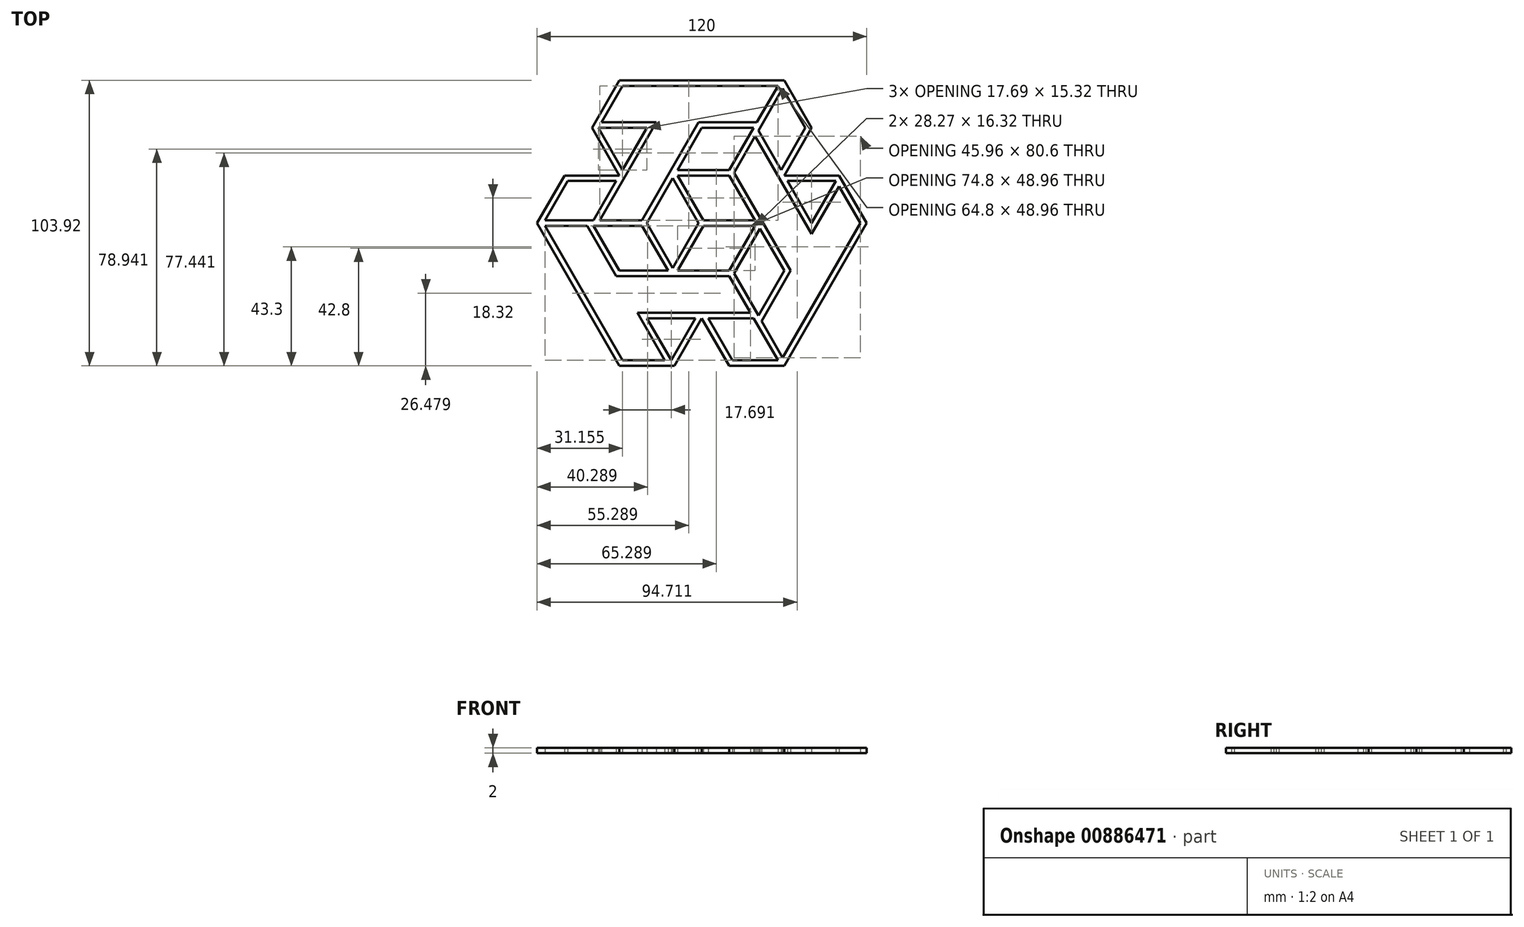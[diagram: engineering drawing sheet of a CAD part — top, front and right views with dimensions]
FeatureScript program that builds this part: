
annotation { "Feature Type Name" : "Feature", "Feature Type Description" : "" }
export const myFeature = defineFeature(function(context is Context, id is Id, definition is map)
    precondition{}
    {
        {
            var Q0;
            Q0=qCreatedBy(makeId("Top.planeOp"),FACE);
            var sketch = newSketch(context, id + "F0", { "sketchPlane" : qUnion([Q0])});
            skCircle(sketch, "E0.cCircle", {"center": v(0, 0) * mm, "radius": 60 * mm, "construction": true});
            skLineSegment(sketch, "E0.0", {"start": v(-60, 0) * mm, "end": v(-50, 17.32) * mm});
            skLineSegment(sketch, "E0.1", {"start": v(-30, 51.96) * mm, "end": v(30, 51.96) * mm});
            skLineSegment(sketch, "E0.2", {"start": v(30, 51.96) * mm, "end": v(60, 0) * mm});
            skLineSegment(sketch, "E0.3", {"start": v(60, 0) * mm, "end": v(30, -51.96) * mm});
            skLineSegment(sketch, "E0.4", {"start": v(30, -51.96) * mm, "end": v(-30, -51.96) * mm});
            skLineSegment(sketch, "E0.5", {"start": v(-30, -51.96) * mm, "end": v(-60, 0) * mm});
            skLineSegment(sketch, "E1", {"start": v(-20, 34.64) * mm, "end": v(-28.85, 19.32) * mm});
            skLineSegment(sketch, "E2", {"start": v(0, 34.64) * mm, "end": v(-8.85, 19.32) * mm});
            skLineSegment(sketch, "E3", {"start": v(-37.7, 34.64) * mm, "end": v(-20, 34.64) * mm});
            skLineSegment(sketch, "E4", {"start": v(-50, 17.32) * mm, "end": v(-30, 17.32) * mm});
            skPoint(sketch, "E5.orphan", {"position": v(-10, 51.96) * mm});
            skPoint(sketch, "E6.orphan", {"position": v(10, 51.96) * mm});
            skLineSegment(sketch, "E7.trimOffspring", {"start": v(0, 34.64) * mm, "end": v(18.85, 34.64) * mm});
            skLineSegment(sketch, "E8.trimOffspring", {"start": v(-8.85, 17.32) * mm, "end": v(10, 17.32) * mm});
            skLineSegment(sketch, "E9", {"start": v(-40, 34.64) * mm, "end": v(-30, 17.32) * mm});
            skLineSegment(sketch, "E10.trimOffspring", {"start": v(-40, 34.64) * mm, "end": v(-30, 51.96) * mm});
            skLineSegment(sketch, "E11.0", {"start": v(-16.54, 36.64) * mm, "end": v(-37.11, 1) * mm});
            skLineSegment(sketch, "E11.1", {"start": v(-36.54, 36.64) * mm, "end": v(-16.54, 36.64) * mm});
            skLineSegment(sketch, "E11.2", {"start": v(-36.54, 36.64) * mm, "end": v(-28.85, 49.96) * mm});
            skLineSegment(sketch, "E11.3", {"start": v(-28.85, 49.96) * mm, "end": v(27.7, 49.96) * mm});
            skLineSegment(sketch, "E12.0", {"start": v(-1.15, 36.64) * mm, "end": v(-21.73, 1) * mm});
            skLineSegment(sketch, "E12.1", {"start": v(-1.15, 36.64) * mm, "end": v(20, 36.64) * mm});
            skLineSegment(sketch, "E13.1", {"start": v(27.7, 49.96) * mm, "end": v(20, 36.64) * mm});
            skLineSegment(sketch, "E14.0", {"start": v(-37.7, 34.64) * mm, "end": v(-28.85, 19.32) * mm});
            skLineSegment(sketch, "E15.0", {"start": v(-10.58, 16.32) * mm, "end": v(-1.15, 0) * mm});
            skLineSegment(sketch, "E16.0", {"start": v(-8.85, 17.32) * mm, "end": v(0.58, 1) * mm});
            skLineSegment(sketch, "E17.trimOffspring", {"start": v(18.85, 34.64) * mm, "end": v(10, 19.32) * mm});
            skLineSegment(sketch, "E18.trimOffspring", {"start": v(-10.58, 16.32) * mm, "end": v(-20, 0) * mm});
            skLineSegment(sketch, "E19.0", {"start": v(-48.85, 15.32) * mm, "end": v(-31.15, 15.32) * mm});
            skLineSegment(sketch, "E19.1", {"start": v(-57.11, 1) * mm, "end": v(-48.85, 15.32) * mm});
            skLineSegment(sketch, "E20.0", {"start": v(-57.11, 1) * mm, "end": v(-39.42, 1) * mm});
            skPoint(sketch, "E21.endSnap0", {"position": v(-38.27, 1) * mm});
            skLineSegment(sketch, "E22.0", {"start": v(-8.85, 19.32) * mm, "end": v(10, 19.32) * mm});
            skLineSegment(sketch, "E23.trimOffspring", {"start": v(-31.15, 15.32) * mm, "end": v(-39.42, 1) * mm});
            skLineSegment(sketch, "E24.trimOffspring", {"start": v(-37.11, 1) * mm, "end": v(-21.73, 1) * mm});
            skPoint(sketch, "E25.orphan", {"position": v(-19.42, 1) * mm});
            skLineSegment(sketch, "E26.1.0", {"start": v(30, -51.96) * mm, "end": v(10, -17.32) * mm});
            skLineSegment(sketch, "E26.1.1", {"start": v(10, -51.96) * mm, "end": v(0, -34.64) * mm});
            skLineSegment(sketch, "E26.1.2", {"start": v(-11.15, -49.96) * mm, "end": v(-2.3, -34.64) * mm});
            skLineSegment(sketch, "E26.1.3", {"start": v(-10, -51.96) * mm, "end": v(-30, -51.96) * mm});
            skLineSegment(sketch, "E26.1.4", {"start": v(30, -51.96) * mm, "end": v(10, -51.96) * mm});
            skPoint(sketch, "E26.1.5", {"position": v(-50, -17.32) * mm});
            skPoint(sketch, "E26.1.6", {"position": v(8.85, -17.32) * mm});
            skLineSegment(sketch, "E26.1.7", {"start": v(-39.42, -1) * mm, "end": v(-21.73, -1) * mm});
            skLineSegment(sketch, "E26.1.8", {"start": v(27.7, -49.96) * mm, "end": v(11.15, -49.96) * mm});
            skLineSegment(sketch, "E26.1.9", {"start": v(-23.46, -32.64) * mm, "end": v(17.7, -32.64) * mm});
            skLineSegment(sketch, "E26.1.11", {"start": v(-8.85, -17.32) * mm, "end": v(0.58, -1) * mm});
            skLineSegment(sketch, "E26.1.12", {"start": v(-10.58, -16.32) * mm, "end": v(-1.15, 0) * mm});
            skLineSegment(sketch, "E26.1.13", {"start": v(-13.46, -49.96) * mm, "end": v(-23.46, -32.64) * mm});
            skLineSegment(sketch, "E26.1.15", {"start": v(-31.15, -19.32) * mm, "end": v(-41.73, -1) * mm});
            skPoint(sketch, "E26.1.16", {"position": v(-40, -34.64) * mm});
            skLineSegment(sketch, "E26.1.17", {"start": v(-30, -17.32) * mm, "end": v(-12.3, -17.32) * mm});
            skLineSegment(sketch, "E26.1.18", {"start": v(-12.3, -17.32) * mm, "end": v(-21.73, -1) * mm});
            skLineSegment(sketch, "E26.1.19", {"start": v(-31.15, -19.32) * mm, "end": v(10, -19.32) * mm});
            skLineSegment(sketch, "E26.1.20", {"start": v(-10, -51.96) * mm, "end": v(0, -34.64) * mm});
            skLineSegment(sketch, "E26.1.21", {"start": v(11.15, -49.96) * mm, "end": v(2.3, -34.64) * mm});
            skLineSegment(sketch, "E26.1.22", {"start": v(-8.85, -17.32) * mm, "end": v(10, -17.32) * mm});
            skLineSegment(sketch, "E26.1.23", {"start": v(-30, -17.32) * mm, "end": v(-39.42, -1) * mm});
            skLineSegment(sketch, "E26.1.24", {"start": v(-10.58, -16.32) * mm, "end": v(-20, 0) * mm});
            skLineSegment(sketch, "E26.1.25", {"start": v(-20, -34.64) * mm, "end": v(-2.3, -34.64) * mm});
            skLineSegment(sketch, "E26.1.26", {"start": v(27.7, -49.96) * mm, "end": v(18.85, -34.64) * mm});
            skLineSegment(sketch, "E26.1.27", {"start": v(-11.15, -49.96) * mm, "end": v(-20, -34.64) * mm});
            skPoint(sketch, "E26.1.28", {"position": v(18.27, -33.64) * mm});
            skLineSegment(sketch, "E26.1.29", {"start": v(17.7, -32.64) * mm, "end": v(10, -19.32) * mm});
            skLineSegment(sketch, "E26.1.30", {"start": v(-57.11, -1) * mm, "end": v(-41.73, -1) * mm});
            skLineSegment(sketch, "E26.1.31", {"start": v(-13.46, -49.96) * mm, "end": v(-28.85, -49.96) * mm});
            skLineSegment(sketch, "E26.1.32", {"start": v(-28.85, -49.96) * mm, "end": v(-57.11, -1) * mm});
            skLineSegment(sketch, "E26.1.33", {"start": v(2.3, -34.64) * mm, "end": v(18.85, -34.64) * mm});
            skLineSegment(sketch, "E26.2.1", {"start": v(40, 34.64) * mm, "end": v(30, 17.32) * mm});
            skLineSegment(sketch, "E26.2.2", {"start": v(48.85, 15.32) * mm, "end": v(31.15, 15.32) * mm});
            skLineSegment(sketch, "E26.2.3", {"start": v(50, 17.32) * mm, "end": v(60, 0) * mm});
            skLineSegment(sketch, "E26.2.4", {"start": v(30, 51.96) * mm, "end": v(40, 34.64) * mm});
            skPoint(sketch, "E26.2.5", {"position": v(40, -34.64) * mm});
            skPoint(sketch, "E26.2.6", {"position": v(10.58, 16.32) * mm});
            skLineSegment(sketch, "E26.2.7", {"start": v(20.58, -33.64) * mm, "end": v(11.73, -18.32) * mm});
            skLineSegment(sketch, "E26.2.8", {"start": v(29.42, 48.96) * mm, "end": v(37.7, 34.64) * mm});
            skLineSegment(sketch, "E26.2.9", {"start": v(40, -4) * mm, "end": v(19.42, 31.64) * mm});
            skLineSegment(sketch, "E26.2.11", {"start": v(19.42, 1) * mm, "end": v(0.58, 1) * mm});
            skLineSegment(sketch, "E26.2.12", {"start": v(19.42, -1) * mm, "end": v(0.58, -1) * mm});
            skLineSegment(sketch, "E26.2.13", {"start": v(50, 13.32) * mm, "end": v(40, -4) * mm});
            skLineSegment(sketch, "E26.2.14", {"start": v(30, -51.96) * mm, "end": v(10, -17.32) * mm});
            skLineSegment(sketch, "E26.2.15", {"start": v(32.3, -17.32) * mm, "end": v(21.73, -35.64) * mm});
            skPoint(sketch, "E26.2.16", {"position": v(50, -17.32) * mm});
            skLineSegment(sketch, "E26.2.17", {"start": v(30, -17.32) * mm, "end": v(21.15, -2) * mm});
            skLineSegment(sketch, "E26.2.18", {"start": v(21.15, -2) * mm, "end": v(11.73, -18.32) * mm});
            skLineSegment(sketch, "E26.2.19", {"start": v(32.3, -17.32) * mm, "end": v(11.73, 18.32) * mm});
            skLineSegment(sketch, "E26.2.20", {"start": v(50, 17.32) * mm, "end": v(30, 17.32) * mm});
            skLineSegment(sketch, "E26.2.21", {"start": v(37.7, 34.64) * mm, "end": v(28.85, 19.32) * mm});
            skLineSegment(sketch, "E26.2.22", {"start": v(19.42, 1) * mm, "end": v(10, 17.32) * mm});
            skLineSegment(sketch, "E26.2.23", {"start": v(30, -17.32) * mm, "end": v(20.58, -33.64) * mm});
            skLineSegment(sketch, "E26.2.24", {"start": v(19.42, -1) * mm, "end": v(10, -17.32) * mm});
            skLineSegment(sketch, "E26.2.25", {"start": v(40, 0) * mm, "end": v(31.15, 15.32) * mm});
            skLineSegment(sketch, "E26.2.26", {"start": v(29.42, 48.96) * mm, "end": v(20.58, 33.64) * mm});
            skLineSegment(sketch, "E26.2.27", {"start": v(48.85, 15.32) * mm, "end": v(40, 0) * mm});
            skPoint(sketch, "E26.2.28", {"position": v(20, 32.64) * mm});
            skLineSegment(sketch, "E26.2.29", {"start": v(19.42, 31.64) * mm, "end": v(11.73, 18.32) * mm});
            skLineSegment(sketch, "E26.2.30", {"start": v(29.42, -48.96) * mm, "end": v(21.73, -35.64) * mm});
            skLineSegment(sketch, "E26.2.31", {"start": v(50, 13.32) * mm, "end": v(57.7, 0) * mm});
            skLineSegment(sketch, "E26.2.32", {"start": v(57.7, 0) * mm, "end": v(29.42, -48.96) * mm});
            skLineSegment(sketch, "E26.2.33", {"start": v(28.85, 19.32) * mm, "end": v(20.58, 33.64) * mm});
            skSolve(sketch);
        }
        {
            var Q0;
            Q0=makeQuery(id+"F0.imprint","IMPRINT",FACE,{"disambiguationData":[TD([[makeQuery(id+"F0.imprint","IMPRINT",EDGE,{"derivedFrom":sQuery(id+"F0.wireOp",EDGE,"E0.0")}),-1.0]])]});
            extrude(context, id + "F1", {"entities" : qUnion([Q0]), "depth" : 2 * mm, "offsetDistance" : 25 * mm});
        }
    });
